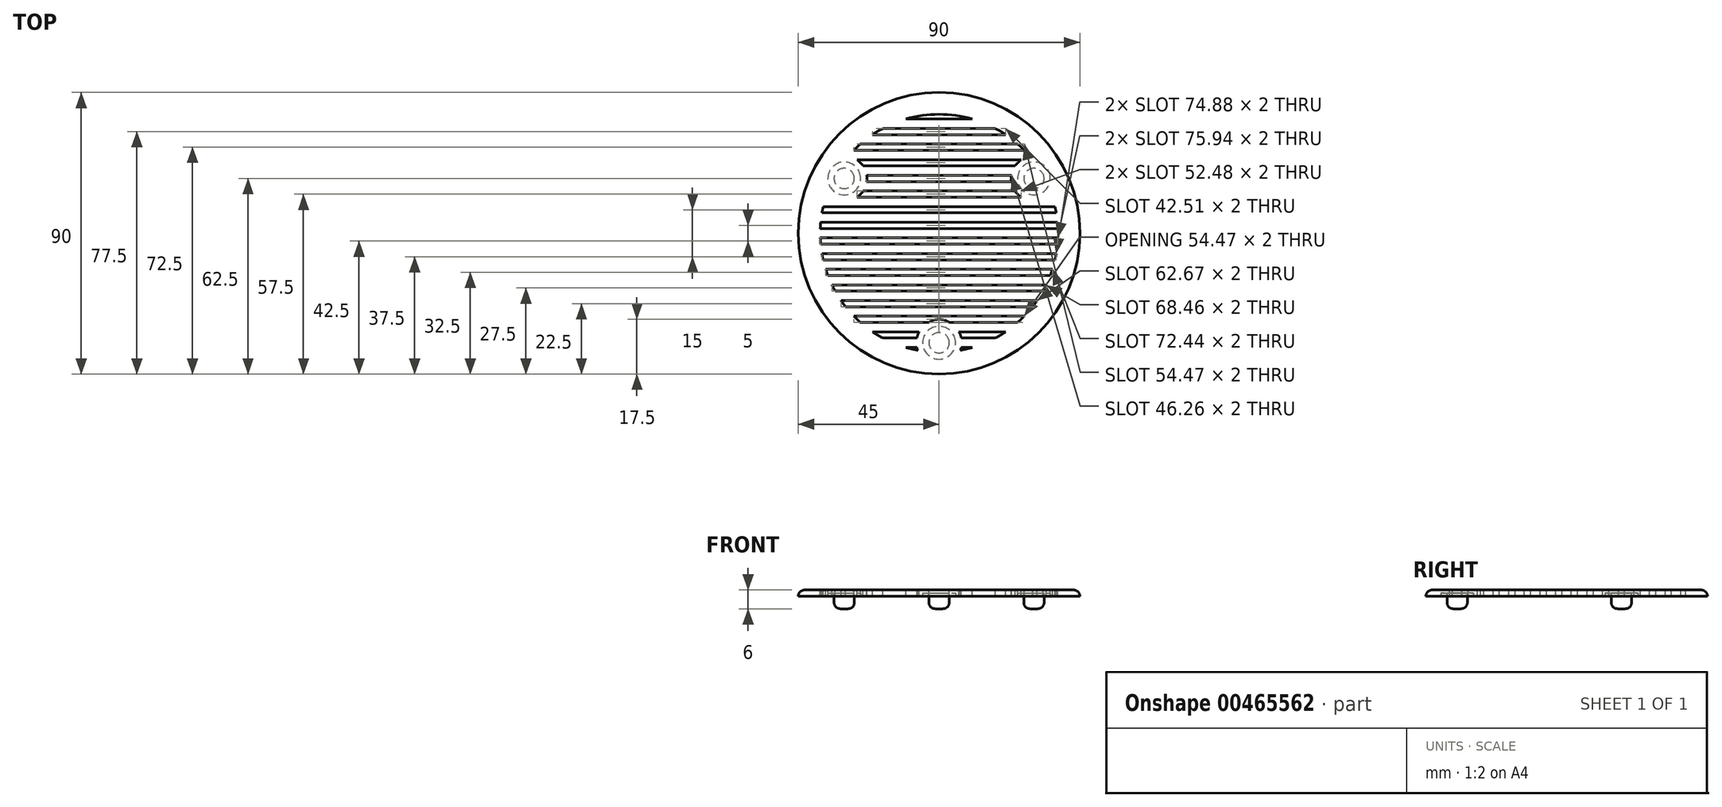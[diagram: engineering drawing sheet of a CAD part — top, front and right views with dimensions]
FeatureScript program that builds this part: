
annotation { "Feature Type Name" : "Feature", "Feature Type Description" : "" }
export const myFeature = defineFeature(function(context is Context, id is Id, definition is map)
    precondition{}
    {
        {
            var Q0;
            Q0=qCreatedBy(makeId("Top.planeOp"),FACE);
            var sketch = newSketch(context, id + "F0", { "sketchPlane" : qUnion([Q0])});
            skCircle(sketch, "E0", {"center": v(0, 0) * mm, "radius": 45 * mm});
            skSolve(sketch);
        }
        {
            var Q0;
            Q0=makeQuery(id+"F0.imprint","IMPRINT",FACE,{"disambiguationData":[TD([[makeQuery(id+"F0.imprint","IMPRINT",EDGE,{"derivedFrom":sQuery(id+"F0.wireOp",EDGE,"E0")}),1.0]])]});
            extrude(context, id + "F1", {"entities" : qUnion([Q0]), "depth" : 2 * mm});
        }
        {
            var Q0;
            Q0=makeQuery(id+"F1.opExtrude","CAP_FACE",FACE,{"disambiguationData":[OSD([sQuery(id+"F0.wireOp",EDGE,"E0")])],"isStart":true});
            var sketch = newSketch(context, id + "F2", { "sketchPlane" : qUnion([Q0])});
            skCircle(sketch, "E1", {"center": v(0, 35) * mm, "radius": 5.25 * mm});
            skCircle(sketch, "E2.1.0", {"center": v(-30.31, -17.5) * mm, "radius": 5.25 * mm});
            skCircle(sketch, "E2.2.0", {"center": v(30.31, -17.5) * mm, "radius": 5.25 * mm});
            skPoint(sketch, "E2.center", {"position": v(0, 0) * mm});
            skSolve(sketch);
        }
        {
            var Q0;
            Q0=qSketchRegion(id+"F2",true);
            extrude(context, id + "F3", {"entities" : qUnion([Q0]), "operationType" : NewBodyOperationType.REMOVE, "oppositeDirection" : true, "depth" : 1 * mm});
        }
        {
            var Q0;
            Q0=makeQuery(id+"F3.boolean.opBoolean","COPY",FACE,{"derivedFrom":makeQuery(id+"F3.opExtrude","CAP_FACE",FACE,{"disambiguationData":[OSD([sQuery(id+"F2.wireOp",EDGE,"E1")])],"isStart":false})});
            var sketch = newSketch(context, id + "F4", { "sketchPlane" : qUnion([Q0])});
            skCircle(sketch, "E3", {"center": v(0, 35) * mm, "radius": 3.25 * mm});
            skCircle(sketch, "E4.1.0", {"center": v(-30.31, -17.5) * mm, "radius": 3.25 * mm});
            skCircle(sketch, "E4.2.0", {"center": v(30.31, -17.5) * mm, "radius": 3.25 * mm});
            skPoint(sketch, "E4.center", {"position": v(0, 0) * mm});
            skSolve(sketch);
        }
        {
            var Q0;
            Q0=makeQuery(id+"F4.imprint","IMPRINT",FACE,{"disambiguationData":[TD([[makeQuery(id+"F4.imprint","IMPRINT",EDGE,{"derivedFrom":sQuery(id+"F4.wireOp",EDGE,"E3")}),1.0]])]});
            var Q1;
            Q1=makeQuery(id+"F4.imprint","IMPRINT",FACE,{"disambiguationData":[TD([[makeQuery(id+"F4.imprint","IMPRINT",EDGE,{"derivedFrom":sQuery(id+"F4.wireOp",EDGE,"E4.2.0")}),1.0]])]});
            var Q2;
            Q2=makeQuery(id+"F4.imprint","IMPRINT",FACE,{"disambiguationData":[TD([[makeQuery(id+"F4.imprint","IMPRINT",EDGE,{"derivedFrom":sQuery(id+"F4.wireOp",EDGE,"E4.1.0")}),1.0]])]});
            extrude(context, id + "F5", {"entities" : qUnion([Q0, Q1, Q2]), "operationType" : NewBodyOperationType.ADD, "depth" : 5 * mm});
        }
        {
            var Q0;
            Q0=makeQuery(id+"F5.opExtrude","CAP_FACE",FACE,{"disambiguationData":[OSD([sQuery(id+"F4.wireOp",EDGE,"E4.1.0")])],"isStart":false});
            var Q1;
            Q1=makeQuery(id+"F5.opExtrude","CAP_FACE",FACE,{"disambiguationData":[OSD([sQuery(id+"F4.wireOp",EDGE,"E3")])],"isStart":false});
            var Q2;
            Q2=makeQuery(id+"F5.opExtrude","CAP_FACE",FACE,{"disambiguationData":[OSD([sQuery(id+"F4.wireOp",EDGE,"E4.2.0")])],"isStart":false});
            fillet(context, id + "F6", {"entities" : qUnion([Q0, Q1, Q2]), "radius" : 2 * mm, "tangentPropagation" : true, "allowEdgeOverflow" : false});
        }
        {
            var Q0;
            Q0=makeQuery(id+"F1.opExtrude","CAP_EDGE",EDGE,{"disambiguationData":[OSD([sQuery(id+"F0.wireOp",EDGE,"E0")])],"isStart":false});
            fillet(context, id + "F7", {"entities" : qUnion([Q0]), "radius" : 2 * mm, "tangentPropagation" : true, "allowEdgeOverflow" : false});
        }
        {
            var Q0;
            Q0=makeQuery(id+"F1.opExtrude","CAP_FACE",FACE,{"disambiguationData":[OSD([sQuery(id+"F0.wireOp",EDGE,"E0")])],"isStart":false});
            var sketch = newSketch(context, id + "F8", { "sketchPlane" : qUnion([Q0])});
            skPoint(sketch, "E5.middle", {"position": v(0, -37.5) * mm});
            skPoint(sketch, "E6.0.1.2", {"position": v(0, -32.5) * mm});
            skPoint(sketch, "E6.0.2.2", {"position": v(0, -27.5) * mm});
            skPoint(sketch, "E6.0.3.2", {"position": v(0, -22.5) * mm});
            skPoint(sketch, "E6.0.4.2", {"position": v(0, -17.5) * mm});
            skPoint(sketch, "E6.0.5.2", {"position": v(0, -12.5) * mm});
            skPoint(sketch, "E6.0.6.2", {"position": v(0, -7.5) * mm});
            skPoint(sketch, "E6.0.7.2", {"position": v(0, -2.5) * mm});
            skPoint(sketch, "E6.0.8.2", {"position": v(0, 2.5) * mm});
            skPoint(sketch, "E6.0.9.2", {"position": v(0, 7.5) * mm});
            skPoint(sketch, "E6.0.10.2", {"position": v(0, 12.5) * mm});
            skPoint(sketch, "E6.0.11.2", {"position": v(0, 17.5) * mm});
            skPoint(sketch, "E6.0.12.2", {"position": v(0, 22.5) * mm});
            skPoint(sketch, "E6.0.13.2", {"position": v(0, 27.5) * mm});
            skPoint(sketch, "E6.0.14.2", {"position": v(0, 32.5) * mm});
            skPoint(sketch, "E6.0.15.2", {"position": v(0, 37.5) * mm});
            skArc(sketch, "E7.0", {"start": v(-17.94, 33.5) * mm, "mid": v(-19.62, 32.54) * mm, "end": v(-21.25, 31.5) * mm});
            skLineSegment(sketch, "E8.trimOffspring", {"start": v(-10.57, -36.5) * mm, "end": v(-7.1, -36.5) * mm});
            skLineSegment(sketch, "E9.trimOffspring", {"start": v(-17.94, -33.5) * mm, "end": v(-7.1, -33.5) * mm});
            skLineSegment(sketch, "E10.trimOffspring", {"start": v(-21.25, -31.5) * mm, "end": v(-6.35, -31.5) * mm});
            skLineSegment(sketch, "E11.trimOffspring", {"start": v(-25.13, -28.5) * mm, "end": v(-3.21, -28.5) * mm});
            skLineSegment(sketch, "E12.trimOffspring", {"start": v(-27.24, -26.5) * mm, "end": v(27.24, -26.5) * mm});
            skLineSegment(sketch, "E13.trimOffspring", {"start": v(-29.86, -23.5) * mm, "end": v(29.86, -23.5) * mm});
            skLineSegment(sketch, "E14.trimOffspring", {"start": v(-31.33, -21.5) * mm, "end": v(31.33, -21.5) * mm});
            skLineSegment(sketch, "E15.trimOffspring", {"start": v(-33.2, -18.5) * mm, "end": v(33.2, -18.5) * mm});
            skLineSegment(sketch, "E16.trimOffspring", {"start": v(-34.23, -16.5) * mm, "end": v(34.23, -16.5) * mm});
            skLineSegment(sketch, "E17.trimOffspring", {"start": v(-35.52, -13.5) * mm, "end": v(35.52, -13.5) * mm});
            skLineSegment(sketch, "E18.trimOffspring", {"start": v(-36.22, -11.5) * mm, "end": v(36.22, -11.5) * mm});
            skLineSegment(sketch, "E19.trimOffspring", {"start": v(-37.04, -8.5) * mm, "end": v(37.04, -8.5) * mm});
            skLineSegment(sketch, "E20.trimOffspring", {"start": v(-37.44, -6.5) * mm, "end": v(37.44, -6.5) * mm});
            skLineSegment(sketch, "E21.trimOffspring", {"start": v(-37.84, -3.5) * mm, "end": v(37.84, -3.5) * mm});
            skLineSegment(sketch, "E22.trimOffspring", {"start": v(-37.97, -1.5) * mm, "end": v(37.97, -1.5) * mm});
            skLineSegment(sketch, "E23.trimOffspring", {"start": v(-37.97, 1.5) * mm, "end": v(37.97, 1.5) * mm});
            skLineSegment(sketch, "E24.trimOffspring", {"start": v(-37.84, 3.5) * mm, "end": v(37.84, 3.5) * mm});
            skLineSegment(sketch, "E25.trimOffspring", {"start": v(-37.44, 6.5) * mm, "end": v(37.44, 6.5) * mm});
            skLineSegment(sketch, "E26.trimOffspring", {"start": v(-37.04, 8.5) * mm, "end": v(37.04, 8.5) * mm});
            skLineSegment(sketch, "E27.trimOffspring", {"start": v(-24.26, 13.5) * mm, "end": v(24.26, 13.5) * mm});
            skLineSegment(sketch, "E28.trimOffspring", {"start": v(-23.13, 16.5) * mm, "end": v(23.13, 16.5) * mm});
            skLineSegment(sketch, "E29.trimOffspring", {"start": v(-23.13, 18.5) * mm, "end": v(23.13, 18.5) * mm});
            skLineSegment(sketch, "E30.trimOffspring", {"start": v(-24.26, 21.5) * mm, "end": v(24.26, 21.5) * mm});
            skLineSegment(sketch, "E31.trimOffspring", {"start": v(-26.24, 23.5) * mm, "end": v(26.24, 23.5) * mm});
            skLineSegment(sketch, "E32.trimOffspring", {"start": v(-27.24, 26.5) * mm, "end": v(27.24, 26.5) * mm});
            skLineSegment(sketch, "E33.trimOffspring", {"start": v(-25.13, 28.5) * mm, "end": v(25.13, 28.5) * mm});
            skLineSegment(sketch, "E34.trimOffspring", {"start": v(-21.25, 31.5) * mm, "end": v(21.25, 31.5) * mm});
            skLineSegment(sketch, "E35.trimOffspring", {"start": v(-17.94, 33.5) * mm, "end": v(17.94, 33.5) * mm});
            skLineSegment(sketch, "E36.trimOffspring", {"start": v(-10.57, 36.5) * mm, "end": v(10.57, 36.5) * mm});
            skArc(sketch, "E37.trimOffspring", {"start": v(-25.13, 28.5) * mm, "mid": v(-26.2, 27.52) * mm, "end": v(-27.24, 26.5) * mm});
            skArc(sketch, "E38.trimOffspring", {"start": v(-37.04, 8.5) * mm, "mid": v(-37.25, 7.5) * mm, "end": v(-37.44, 6.5) * mm});
            skArc(sketch, "E39.trimOffspring", {"start": v(-37.84, 3.5) * mm, "mid": v(-37.92, 2.5) * mm, "end": v(-37.97, 1.5) * mm});
            skArc(sketch, "E40.trimOffspring", {"start": v(-37.97, -1.5) * mm, "mid": v(-37.92, -2.5) * mm, "end": v(-37.84, -3.5) * mm});
            skArc(sketch, "E41.trimOffspring", {"start": v(-37.44, -6.5) * mm, "mid": v(-37.25, -7.5) * mm, "end": v(-37.04, -8.5) * mm});
            skArc(sketch, "E42.trimOffspring", {"start": v(-36.22, -11.5) * mm, "mid": v(-35.88, -12.5) * mm, "end": v(-35.52, -13.5) * mm});
            skArc(sketch, "E43.trimOffspring", {"start": v(-34.23, -16.5) * mm, "mid": v(-33.73, -17.5) * mm, "end": v(-33.2, -18.5) * mm});
            skArc(sketch, "E44.trimOffspring", {"start": v(-31.33, -21.5) * mm, "mid": v(-30.61, -22.51) * mm, "end": v(-29.86, -23.5) * mm});
            skArc(sketch, "E45.trimOffspring", {"start": v(-27.24, -26.5) * mm, "mid": v(-26.2, -27.52) * mm, "end": v(-25.13, -28.5) * mm});
            skArc(sketch, "E46.trimOffspring", {"start": v(-21.25, -31.5) * mm, "mid": v(-19.62, -32.54) * mm, "end": v(-17.94, -33.5) * mm});
            skArc(sketch, "E47.trimOffspring", {"start": v(-10.57, -36.5) * mm, "mid": v(-8.72, -36.99) * mm, "end": v(-6.85, -37.38) * mm});
            skArc(sketch, "E48.trimOffspring", {"start": v(10.57, 36.5) * mm, "mid": v(0, 38) * mm, "end": v(-10.57, 36.5) * mm});
            skArc(sketch, "E49.trimOffspring", {"start": v(21.25, 31.5) * mm, "mid": v(19.62, 32.54) * mm, "end": v(17.94, 33.5) * mm});
            skArc(sketch, "E50.trimOffspring", {"start": v(27.24, 26.5) * mm, "mid": v(26.2, 27.52) * mm, "end": v(25.13, 28.5) * mm});
            skArc(sketch, "E51.trimOffspring", {"start": v(37.44, 6.5) * mm, "mid": v(37.25, 7.5) * mm, "end": v(37.04, 8.5) * mm});
            skArc(sketch, "E52.trimOffspring", {"start": v(37.97, 1.5) * mm, "mid": v(37.92, 2.5) * mm, "end": v(37.84, 3.5) * mm});
            skArc(sketch, "E53.trimOffspring", {"start": v(37.84, -3.5) * mm, "mid": v(37.92, -2.5) * mm, "end": v(37.97, -1.5) * mm});
            skArc(sketch, "E54.trimOffspring", {"start": v(37.04, -8.5) * mm, "mid": v(37.25, -7.5) * mm, "end": v(37.44, -6.5) * mm});
            skArc(sketch, "E55.trimOffspring", {"start": v(35.52, -13.5) * mm, "mid": v(35.88, -12.5) * mm, "end": v(36.22, -11.5) * mm});
            skArc(sketch, "E56.trimOffspring", {"start": v(33.2, -18.5) * mm, "mid": v(33.73, -17.5) * mm, "end": v(34.23, -16.5) * mm});
            skArc(sketch, "E57.trimOffspring", {"start": v(29.86, -23.5) * mm, "mid": v(30.61, -22.51) * mm, "end": v(31.33, -21.5) * mm});
            skArc(sketch, "E58.trimOffspring", {"start": v(25.13, -28.5) * mm, "mid": v(26.2, -27.52) * mm, "end": v(27.24, -26.5) * mm});
            skArc(sketch, "E59.trimOffspring", {"start": v(17.94, -33.5) * mm, "mid": v(19.62, -32.54) * mm, "end": v(21.25, -31.5) * mm});
            skArc(sketch, "E60.0", {"start": v(-26.24, 11.5) * mm, "mid": v(-25.15, 12.4) * mm, "end": v(-24.26, 13.5) * mm});
            skLineSegment(sketch, "E61.trimOffspring", {"start": v(-26.24, 11.5) * mm, "end": v(26.24, 11.5) * mm});
            skArc(sketch, "E62.trimOffspring", {"start": v(-23.13, 16.5) * mm, "mid": v(-23.06, 17.5) * mm, "end": v(-23.13, 18.5) * mm});
            skArc(sketch, "E63.trimOffspring", {"start": v(-24.26, 21.5) * mm, "mid": v(-25.15, 22.6) * mm, "end": v(-26.24, 23.5) * mm});
            skLineSegment(sketch, "E64.trimOffspring", {"start": v(3.21, -28.5) * mm, "end": v(25.13, -28.5) * mm});
            skLineSegment(sketch, "E65.trimOffspring", {"start": v(6.35, -31.5) * mm, "end": v(21.25, -31.5) * mm});
            skLineSegment(sketch, "E66.trimOffspring", {"start": v(7.1, -33.5) * mm, "end": v(17.94, -33.5) * mm});
            skLineSegment(sketch, "E67.trimOffspring", {"start": v(7.1, -36.5) * mm, "end": v(10.57, -36.5) * mm});
            skArc(sketch, "E68.trimOffspring", {"start": v(6.85, -37.38) * mm, "mid": v(8.72, -36.99) * mm, "end": v(10.57, -36.5) * mm});
            skArc(sketch, "E69.trimOffspring", {"start": v(-6.35, -31.5) * mm, "mid": v(-6.8, -32.47) * mm, "end": v(-7.1, -33.5) * mm});
            skArc(sketch, "E70.trimOffspring", {"start": v(-7.1, -36.5) * mm, "mid": v(-6.98, -36.94) * mm, "end": v(-6.85, -37.38) * mm});
            skArc(sketch, "E71.trimOffspring", {"start": v(7.1, -33.5) * mm, "mid": v(6.8, -32.47) * mm, "end": v(6.35, -31.5) * mm});
            skArc(sketch, "E72.trimOffspring", {"start": v(6.85, -37.38) * mm, "mid": v(6.98, -36.94) * mm, "end": v(7.1, -36.5) * mm});
            skArc(sketch, "E73.trimOffspring", {"start": v(24.26, 13.5) * mm, "mid": v(25.15, 12.4) * mm, "end": v(26.24, 11.5) * mm});
            skArc(sketch, "E74.trimOffspring", {"start": v(23.13, 18.5) * mm, "mid": v(23.06, 17.5) * mm, "end": v(23.13, 16.5) * mm});
            skArc(sketch, "E75.trimOffspring", {"start": v(26.24, 23.5) * mm, "mid": v(25.15, 22.6) * mm, "end": v(24.26, 21.5) * mm});
            skArc(sketch, "E76", {"start": v(3.21, -28.5) * mm, "mid": v(0, -27.5) * mm, "end": v(-3.21, -28.5) * mm});
            skSolve(sketch);
        }
        {
            var Q0;
            Q0 = qSketchRegion(id + "F8", true);
            extrude(context, id + "F9", {"entities" : qUnion([Q0]), "operationType" : NewBodyOperationType.REMOVE, "oppositeDirection" : true, "depth" : 25 * mm, "offsetDistance" : 25 * mm});
        }
    });
